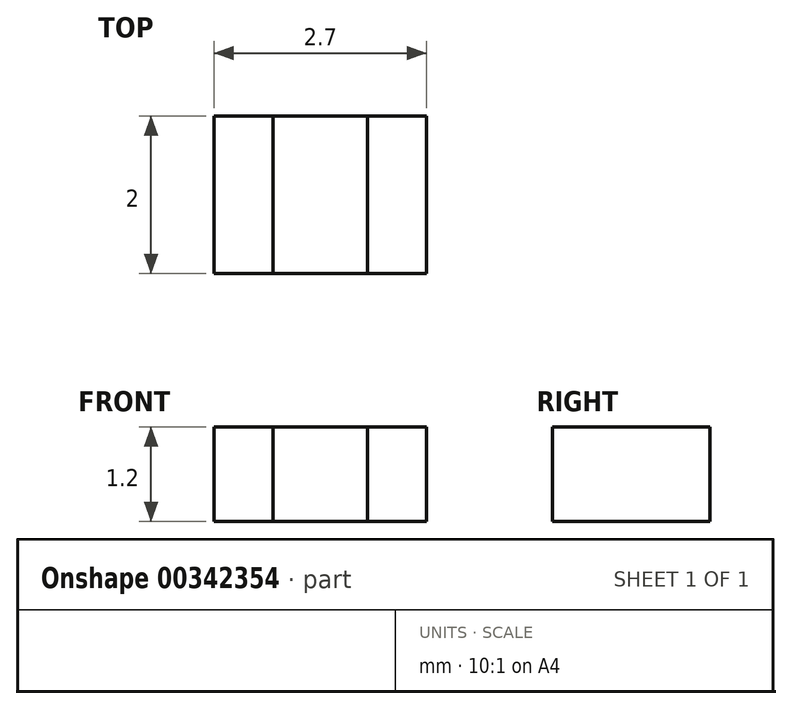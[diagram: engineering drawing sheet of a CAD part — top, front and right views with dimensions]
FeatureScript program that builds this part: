
annotation { "Feature Type Name" : "Feature", "Feature Type Description" : "" }
export const myFeature = defineFeature(function(context is Context, id is Id, definition is map)
    precondition{}
    {
        {
            var Q0;
            Q0=qCreatedBy(makeId("Top.planeOp"),FACE);
            var sketch = newSketch(context, id + "F0", { "sketchPlane" : qUnion([Q0])});
            skLineSegment(sketch, "E0.bottom", {"start": v(0.6, -1) * mm, "end": v(-0.6, -1) * mm});
            skLineSegment(sketch, "E0.top", {"start": v(0.6, 1) * mm, "end": v(-0.6, 1) * mm});
            skLineSegment(sketch, "E0.left", {"start": v(0.6, -1) * mm, "end": v(0.6, 1) * mm});
            skLineSegment(sketch, "E0.right", {"start": v(-0.6, -1) * mm, "end": v(-0.6, 1) * mm});
            skPoint(sketch, "E0.middle", {"position": v(0, 0) * mm});
            skSolve(sketch);
        }
        {
            var Q0;
            Q0=makeQuery(id+"F0.imprint","IMPRINT",FACE,{"disambiguationData":[TD([[makeQuery(id+"F0.imprint","IMPRINT",EDGE,{"derivedFrom":sQuery(id+"F0.wireOp",EDGE,"E0.bottom")}),-1.0]])]});
            extrude(context, id + "F1", {"entities" : qUnion([Q0]), "depth" : 1.2 * mm});
        }
        {
            var Q0;
            Q0=qCreatedBy(makeId("Top.planeOp"),FACE);
            var sketch = newSketch(context, id + "F2", { "sketchPlane" : qUnion([Q0])});
            skLineSegment(sketch, "E1.0", {"start": v(-0.6, -1) * mm, "end": v(-0.6, 1) * mm});
            skLineSegment(sketch, "E2.0", {"start": v(0.6, -1) * mm, "end": v(0.6, 1) * mm});
            skLineSegment(sketch, "E3.bottom", {"start": v(0.6, -1) * mm, "end": v(1.35, -1) * mm});
            skLineSegment(sketch, "E3.top", {"start": v(0.6, 1) * mm, "end": v(1.35, 1) * mm});
            skLineSegment(sketch, "E3.right", {"start": v(1.35, -1) * mm, "end": v(1.35, 1) * mm});
            skLineSegment(sketch, "E4.bottom", {"start": v(-0.6, -1) * mm, "end": v(-1.35, -1) * mm});
            skLineSegment(sketch, "E4.top", {"start": v(-0.6, 1) * mm, "end": v(-1.35, 1) * mm});
            skLineSegment(sketch, "E4.right", {"start": v(-1.35, -1) * mm, "end": v(-1.35, 1) * mm});
            skSolve(sketch);
        }
        {
            var Q0;
            Q0=makeQuery(id+"F2.imprint","IMPRINT",FACE,{"disambiguationData":[TD([[makeQuery(id+"F2.imprint","IMPRINT",EDGE,{"derivedFrom":sQuery(id+"F2.wireOp",EDGE,"E4.bottom")}),-1.0]])]});
            var Q1;
            Q1=makeQuery(id+"F2.imprint","IMPRINT",FACE,{"disambiguationData":[TD([[makeQuery(id+"F2.imprint","IMPRINT",EDGE,{"derivedFrom":sQuery(id+"F2.wireOp",EDGE,"E3.bottom")}),1.0]])]});
            extrude(context, id + "F3", {"entities" : qUnion([Q0, Q1]), "depth" : 1.2 * mm});
        }
    });
